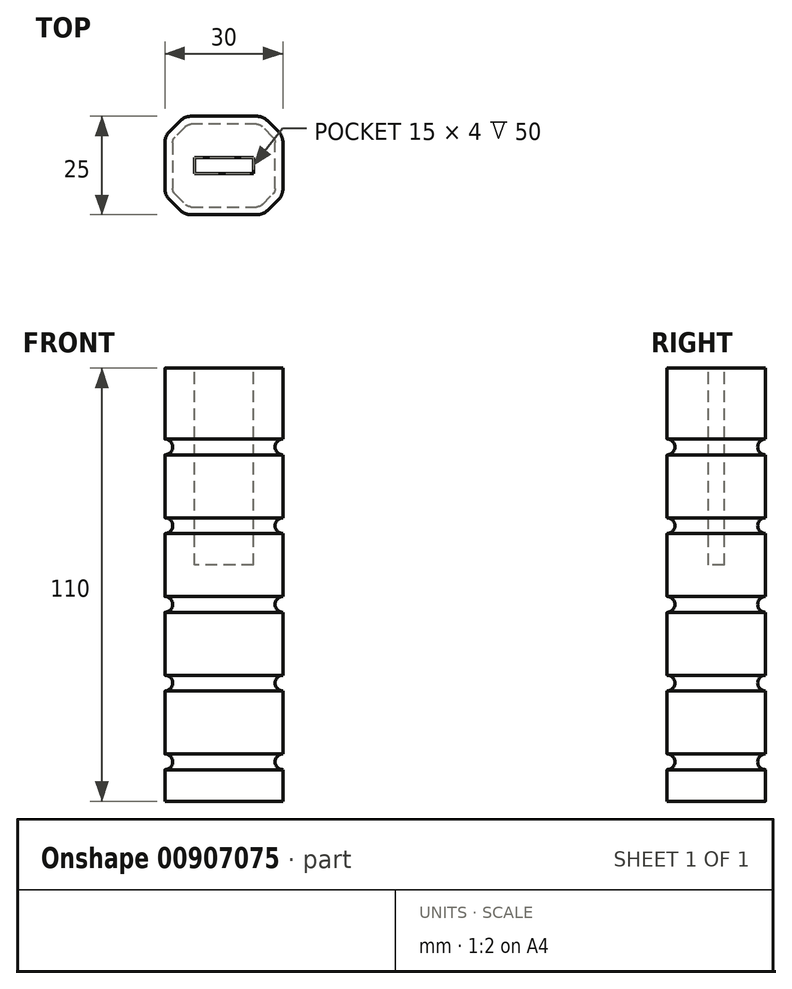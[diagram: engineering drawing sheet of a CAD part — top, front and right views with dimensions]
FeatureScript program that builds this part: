
annotation { "Feature Type Name" : "Feature", "Feature Type Description" : "" }
export const myFeature = defineFeature(function(context is Context, id is Id, definition is map)
    precondition{}
    {
        {
            var Q0;
            Q0=qCreatedBy(makeId("Top.planeOp"),FACE);
            var sketch = newSketch(context, id + "F0", { "sketchPlane" : qUnion([Q0])});
            skLineSegment(sketch, "E0.bottom", {"start": v(15, 12.5) * mm, "end": v(-15, 12.5) * mm});
            skLineSegment(sketch, "E0.top", {"start": v(15, -12.5) * mm, "end": v(-15, -12.5) * mm});
            skLineSegment(sketch, "E0.left", {"start": v(15, 12.5) * mm, "end": v(15, -12.5) * mm});
            skLineSegment(sketch, "E0.right", {"start": v(-15, 12.5) * mm, "end": v(-15, -12.5) * mm});
            skPoint(sketch, "E0.middle", {"position": v(0, 0) * mm});
            skSolve(sketch);
        }
        {
            var Q0;
            Q0 = qSketchRegion(id + "F0", true);
            extrude(context, id + "F1", {"entities" : qUnion([Q0]), "depth" : 110 * mm, "offsetDistance" : 25 * mm});
        }
        {
            var Q0;
            Q0=makeQuery(id+"F1.opExtrude","SWEPT_EDGE",EDGE,{"disambiguationData":[OSD([sQuery(id+"F0.wireOp",EDGE,"E0.top"),sQuery(id+"F0.wireOp",EDGE,"E0.right")])]});
            var Q1;
            Q1=makeQuery(id+"F1.opExtrude","SWEPT_EDGE",EDGE,{"disambiguationData":[OSD([sQuery(id+"F0.wireOp",EDGE,"E0.bottom"),sQuery(id+"F0.wireOp",EDGE,"E0.right")])]});
            var Q2;
            Q2=makeQuery(id+"F1.opExtrude","SWEPT_EDGE",EDGE,{"disambiguationData":[OSD([sQuery(id+"F0.wireOp",EDGE,"E0.top"),sQuery(id+"F0.wireOp",EDGE,"E0.left")])]});
            var Q3;
            Q3=makeQuery(id+"F1.opExtrude","SWEPT_EDGE",EDGE,{"disambiguationData":[OSD([sQuery(id+"F0.wireOp",EDGE,"E0.bottom"),sQuery(id+"F0.wireOp",EDGE,"E0.left")])]});
            chamfer(context, id + "F2", {"entities" : qUnion([Q0, Q1, Q2, Q3]), "width" : 5 * mm, "tangentPropagation" : true});
        }
        {
            var Q0;
            {var subQ0=sQuery(id+"F0.wireOp",EDGE,"E0.top");Q0=makeQuery(id+"F2.opChamfer","BLEND_EDGE",EDGE,{"blendedFrom":[makeQuery(id+"F1.opExtrude","SWEPT_EDGE",EDGE,{"disambiguationData":[OSD([subQ0,sQuery(id+"F0.wireOp",EDGE,"E0.left")])]}),makeQuery(id+"F1.opExtrude","SWEPT_FACE",FACE,{"disambiguationData":[OSD([subQ0])]})],"blendedInto":[makeQuery(id+"F1.opExtrude","SWEPT_FACE",FACE,{"disambiguationData":[OSD([subQ0])]})]});}
            var Q1;
            {var subQ0=sQuery(id+"F0.wireOp",EDGE,"E0.left");Q1=makeQuery(id+"F2.opChamfer","BLEND_EDGE",EDGE,{"blendedFrom":[makeQuery(id+"F1.opExtrude","SWEPT_EDGE",EDGE,{"disambiguationData":[OSD([sQuery(id+"F0.wireOp",EDGE,"E0.top"),subQ0])]}),makeQuery(id+"F1.opExtrude","SWEPT_FACE",FACE,{"disambiguationData":[OSD([subQ0])]})],"blendedInto":[makeQuery(id+"F1.opExtrude","SWEPT_FACE",FACE,{"disambiguationData":[OSD([subQ0])]})]});}
            var Q2;
            {var subQ0=sQuery(id+"F0.wireOp",EDGE,"E0.top");Q2=makeQuery(id+"F2.opChamfer","BLEND_EDGE",EDGE,{"blendedFrom":[makeQuery(id+"F1.opExtrude","SWEPT_EDGE",EDGE,{"disambiguationData":[OSD([subQ0,sQuery(id+"F0.wireOp",EDGE,"E0.right")])]}),makeQuery(id+"F1.opExtrude","SWEPT_FACE",FACE,{"disambiguationData":[OSD([subQ0])]})],"blendedInto":[makeQuery(id+"F1.opExtrude","SWEPT_FACE",FACE,{"disambiguationData":[OSD([subQ0])]})]});}
            var Q3;
            {var subQ0=sQuery(id+"F0.wireOp",EDGE,"E0.right");Q3=makeQuery(id+"F2.opChamfer","BLEND_EDGE",EDGE,{"blendedFrom":[makeQuery(id+"F1.opExtrude","SWEPT_EDGE",EDGE,{"disambiguationData":[OSD([sQuery(id+"F0.wireOp",EDGE,"E0.top"),subQ0])]}),makeQuery(id+"F1.opExtrude","SWEPT_FACE",FACE,{"disambiguationData":[OSD([subQ0])]})],"blendedInto":[makeQuery(id+"F1.opExtrude","SWEPT_FACE",FACE,{"disambiguationData":[OSD([subQ0])]})]});}
            var Q4;
            {var subQ0=sQuery(id+"F0.wireOp",EDGE,"E0.right");Q4=makeQuery(id+"F2.opChamfer","BLEND_EDGE",EDGE,{"blendedFrom":[makeQuery(id+"F1.opExtrude","SWEPT_EDGE",EDGE,{"disambiguationData":[OSD([sQuery(id+"F0.wireOp",EDGE,"E0.bottom"),subQ0])]}),makeQuery(id+"F1.opExtrude","SWEPT_FACE",FACE,{"disambiguationData":[OSD([subQ0])]})],"blendedInto":[makeQuery(id+"F1.opExtrude","SWEPT_FACE",FACE,{"disambiguationData":[OSD([subQ0])]})]});}
            var Q5;
            {var subQ0=sQuery(id+"F0.wireOp",EDGE,"E0.bottom");Q5=makeQuery(id+"F2.opChamfer","BLEND_EDGE",EDGE,{"blendedFrom":[makeQuery(id+"F1.opExtrude","SWEPT_EDGE",EDGE,{"disambiguationData":[OSD([subQ0,sQuery(id+"F0.wireOp",EDGE,"E0.right")])]}),makeQuery(id+"F1.opExtrude","SWEPT_FACE",FACE,{"disambiguationData":[OSD([subQ0])]})],"blendedInto":[makeQuery(id+"F1.opExtrude","SWEPT_FACE",FACE,{"disambiguationData":[OSD([subQ0])]})]});}
            var Q6;
            {var subQ0=sQuery(id+"F0.wireOp",EDGE,"E0.bottom");Q6=makeQuery(id+"F2.opChamfer","BLEND_EDGE",EDGE,{"blendedFrom":[makeQuery(id+"F1.opExtrude","SWEPT_EDGE",EDGE,{"disambiguationData":[OSD([subQ0,sQuery(id+"F0.wireOp",EDGE,"E0.left")])]}),makeQuery(id+"F1.opExtrude","SWEPT_FACE",FACE,{"disambiguationData":[OSD([subQ0])]})],"blendedInto":[makeQuery(id+"F1.opExtrude","SWEPT_FACE",FACE,{"disambiguationData":[OSD([subQ0])]})]});}
            var Q7;
            {var subQ0=sQuery(id+"F0.wireOp",EDGE,"E0.left");Q7=makeQuery(id+"F2.opChamfer","BLEND_EDGE",EDGE,{"blendedFrom":[makeQuery(id+"F1.opExtrude","SWEPT_EDGE",EDGE,{"disambiguationData":[OSD([sQuery(id+"F0.wireOp",EDGE,"E0.bottom"),subQ0])]}),makeQuery(id+"F1.opExtrude","SWEPT_FACE",FACE,{"disambiguationData":[OSD([subQ0])]})],"blendedInto":[makeQuery(id+"F1.opExtrude","SWEPT_FACE",FACE,{"disambiguationData":[OSD([subQ0])]})]});}
            fillet(context, id + "F3", {"entities" : qUnion([Q0, Q1, Q2, Q3, Q4, Q5, Q6, Q7]), "radius" : 4 * mm, "tangentPropagation" : true, "allowEdgeOverflow" : false});
        }
        {
            var Q0;
            Q0=makeQuery(id+"F1.opExtrude","CAP_FACE",FACE,{"disambiguationData":[OSD([sQuery(id+"F0.wireOp",EDGE,"E0.bottom"),sQuery(id+"F0.wireOp",EDGE,"E0.top"),sQuery(id+"F0.wireOp",EDGE,"E0.left"),sQuery(id+"F0.wireOp",EDGE,"E0.right")])],"isStart":false});
            var sketch = newSketch(context, id + "F4", { "sketchPlane" : qUnion([Q0])});
            skLineSegment(sketch, "E1.bottom", {"start": v(7.5, 2) * mm, "end": v(-7.5, 2) * mm});
            skLineSegment(sketch, "E1.top", {"start": v(7.5, -2) * mm, "end": v(-7.5, -2) * mm});
            skLineSegment(sketch, "E1.left", {"start": v(7.5, 2) * mm, "end": v(7.5, -2) * mm});
            skLineSegment(sketch, "E1.right", {"start": v(-7.5, 2) * mm, "end": v(-7.5, -2) * mm});
            skPoint(sketch, "E1.middle", {"position": v(0, 0) * mm});
            skSolve(sketch);
        }
        {
            var Q0;
            Q0 = qSketchRegion(id + "F4", true);
            extrude(context, id + "F5", {"entities" : qUnion([Q0]), "operationType" : NewBodyOperationType.REMOVE, "oppositeDirection" : true, "depth" : 50 * mm, "offsetDistance" : 25 * mm});
        }
        {
            var Q0;
            Q0=makeQuery(id+"F1.opExtrude","CAP_FACE",FACE,{"disambiguationData":[OSD([sQuery(id+"F0.wireOp",EDGE,"E0.bottom"),sQuery(id+"F0.wireOp",EDGE,"E0.top"),sQuery(id+"F0.wireOp",EDGE,"E0.left"),sQuery(id+"F0.wireOp",EDGE,"E0.right")])],"isStart":false});
            cPlane(context, id + "F6", {"entities" : qUnion([Q0]), "cplaneType" : CPlaneType.OFFSET, "offset" : 20 * mm, "oppositeDirection" : true, "width" : 150 * mm, "height" : 150 * mm});
        }
        {
            var Q0;
            Q0=qCreatedBy(id+"F6.planeOp",FACE);
            cPlane(context, id + "F7", {"entities" : qUnion([Q0]), "cplaneType" : CPlaneType.OFFSET, "offset" : 20 * mm, "oppositeDirection" : true, "width" : 150 * mm, "height" : 150 * mm});
        }
        {
            var Q0;
            Q0=qCreatedBy(id+"F7.planeOp",FACE);
            cPlane(context, id + "F8", {"entities" : qUnion([Q0]), "cplaneType" : CPlaneType.OFFSET, "offset" : 20 * mm, "oppositeDirection" : true, "width" : 150 * mm, "height" : 150 * mm});
        }
        {
            var Q0;
            Q0=qCreatedBy(id+"F8.planeOp",FACE);
            cPlane(context, id + "F9", {"entities" : qUnion([Q0]), "cplaneType" : CPlaneType.OFFSET, "offset" : 20 * mm, "oppositeDirection" : true, "width" : 150 * mm, "height" : 150 * mm});
        }
        {
            var Q0;
            Q0=qCreatedBy(id+"F9.planeOp",FACE);
            cPlane(context, id + "F10", {"entities" : qUnion([Q0]), "cplaneType" : CPlaneType.OFFSET, "offset" : 20 * mm, "oppositeDirection" : true, "width" : 150 * mm, "height" : 150 * mm});
        }
        {
            var Q0;
            Q0=qCreatedBy(id+"F6.planeOp",FACE);
            var sketch = newSketch(context, id + "F11", { "sketchPlane" : qUnion([Q0])});
            skLineSegment(sketch, "E2.0.0", {"start": v(-11.17, 11.33) * mm, "end": v(-13.83, 8.67) * mm});
            skArc(sketch, "E2.0.1", {"start": v(-13.83, 8.67) * mm, "mid": v(-14.7, 7.37) * mm, "end": v(-15, 5.84) * mm});
            skLineSegment(sketch, "E2.0.2", {"start": v(-15, 5.84) * mm, "end": v(-15, -5.84) * mm});
            skArc(sketch, "E2.0.3", {"start": v(-15, -5.84) * mm, "mid": v(-14.7, -7.37) * mm, "end": v(-13.83, -8.67) * mm});
            skLineSegment(sketch, "E2.0.4", {"start": v(-13.83, -8.67) * mm, "end": v(-11.17, -11.33) * mm});
            skArc(sketch, "E2.0.5", {"start": v(-11.17, -11.33) * mm, "mid": v(-9.87, -12.2) * mm, "end": v(-8.34, -12.5) * mm});
            skLineSegment(sketch, "E2.0.6", {"start": v(-8.34, -12.5) * mm, "end": v(8.34, -12.5) * mm});
            skArc(sketch, "E2.0.7", {"start": v(8.34, -12.5) * mm, "mid": v(9.87, -12.2) * mm, "end": v(11.17, -11.33) * mm});
            skLineSegment(sketch, "E2.0.8", {"start": v(11.17, -11.33) * mm, "end": v(13.83, -8.67) * mm});
            skArc(sketch, "E2.0.9", {"start": v(13.83, -8.67) * mm, "mid": v(14.7, -7.37) * mm, "end": v(15, -5.84) * mm});
            skLineSegment(sketch, "E2.0.10", {"start": v(15, -5.84) * mm, "end": v(15, 5.84) * mm});
            skArc(sketch, "E2.0.11", {"start": v(15, 5.84) * mm, "mid": v(14.7, 7.37) * mm, "end": v(13.83, 8.67) * mm});
            skLineSegment(sketch, "E2.0.12", {"start": v(13.83, 8.67) * mm, "end": v(11.17, 11.33) * mm});
            skArc(sketch, "E2.0.13", {"start": v(11.17, 11.33) * mm, "mid": v(9.87, 12.2) * mm, "end": v(8.34, 12.5) * mm});
            skLineSegment(sketch, "E2.0.14", {"start": v(8.34, 12.5) * mm, "end": v(-8.34, 12.5) * mm});
            skArc(sketch, "E2.0.15", {"start": v(-8.34, 12.5) * mm, "mid": v(-9.87, 12.2) * mm, "end": v(-11.17, 11.33) * mm});
            skSolve(sketch);
        }
        {
            var Q0;
            Q0=qCreatedBy(id+"F7.planeOp",FACE);
            var sketch = newSketch(context, id + "F12", { "sketchPlane" : qUnion([Q0])});
            skLineSegment(sketch, "E3.0.0", {"start": v(-11.17, 11.33) * mm, "end": v(-13.83, 8.67) * mm});
            skArc(sketch, "E3.0.1", {"start": v(-13.83, 8.67) * mm, "mid": v(-14.7, 7.37) * mm, "end": v(-15, 5.84) * mm});
            skLineSegment(sketch, "E3.0.2", {"start": v(-15, 5.84) * mm, "end": v(-15, -5.84) * mm});
            skArc(sketch, "E3.0.3", {"start": v(-15, -5.84) * mm, "mid": v(-14.7, -7.37) * mm, "end": v(-13.83, -8.67) * mm});
            skLineSegment(sketch, "E3.0.4", {"start": v(-13.83, -8.67) * mm, "end": v(-11.17, -11.33) * mm});
            skArc(sketch, "E3.0.5", {"start": v(-11.17, -11.33) * mm, "mid": v(-9.87, -12.2) * mm, "end": v(-8.34, -12.5) * mm});
            skLineSegment(sketch, "E3.0.6", {"start": v(-8.34, -12.5) * mm, "end": v(8.34, -12.5) * mm});
            skArc(sketch, "E3.0.7", {"start": v(8.34, -12.5) * mm, "mid": v(9.87, -12.2) * mm, "end": v(11.17, -11.33) * mm});
            skLineSegment(sketch, "E3.0.8", {"start": v(11.17, -11.33) * mm, "end": v(13.83, -8.67) * mm});
            skArc(sketch, "E3.0.9", {"start": v(13.83, -8.67) * mm, "mid": v(14.7, -7.37) * mm, "end": v(15, -5.84) * mm});
            skLineSegment(sketch, "E3.0.10", {"start": v(15, -5.84) * mm, "end": v(15, 5.84) * mm});
            skArc(sketch, "E3.0.11", {"start": v(15, 5.84) * mm, "mid": v(14.7, 7.37) * mm, "end": v(13.83, 8.67) * mm});
            skLineSegment(sketch, "E3.0.12", {"start": v(13.83, 8.67) * mm, "end": v(11.17, 11.33) * mm});
            skArc(sketch, "E3.0.13", {"start": v(11.17, 11.33) * mm, "mid": v(9.87, 12.2) * mm, "end": v(8.34, 12.5) * mm});
            skLineSegment(sketch, "E3.0.14", {"start": v(8.34, 12.5) * mm, "end": v(-8.34, 12.5) * mm});
            skArc(sketch, "E3.0.15", {"start": v(-8.34, 12.5) * mm, "mid": v(-9.87, 12.2) * mm, "end": v(-11.17, 11.33) * mm});
            skSolve(sketch);
        }
        {
            var Q0;
            Q0=qCreatedBy(id+"F8.planeOp",FACE);
            var sketch = newSketch(context, id + "F13", { "sketchPlane" : qUnion([Q0])});
            skLineSegment(sketch, "E4.0.0", {"start": v(-11.17, 11.33) * mm, "end": v(-13.83, 8.67) * mm});
            skArc(sketch, "E4.0.1", {"start": v(-13.83, 8.67) * mm, "mid": v(-14.7, 7.37) * mm, "end": v(-15, 5.84) * mm});
            skLineSegment(sketch, "E4.0.2", {"start": v(-15, 5.84) * mm, "end": v(-15, -5.84) * mm});
            skArc(sketch, "E4.0.3", {"start": v(-15, -5.84) * mm, "mid": v(-14.7, -7.37) * mm, "end": v(-13.83, -8.67) * mm});
            skLineSegment(sketch, "E4.0.4", {"start": v(-13.83, -8.67) * mm, "end": v(-11.17, -11.33) * mm});
            skArc(sketch, "E4.0.5", {"start": v(-11.17, -11.33) * mm, "mid": v(-9.87, -12.2) * mm, "end": v(-8.34, -12.5) * mm});
            skLineSegment(sketch, "E4.0.6", {"start": v(-8.34, -12.5) * mm, "end": v(8.34, -12.5) * mm});
            skArc(sketch, "E4.0.7", {"start": v(8.34, -12.5) * mm, "mid": v(9.87, -12.2) * mm, "end": v(11.17, -11.33) * mm});
            skLineSegment(sketch, "E4.0.8", {"start": v(11.17, -11.33) * mm, "end": v(13.83, -8.67) * mm});
            skArc(sketch, "E4.0.9", {"start": v(13.83, -8.67) * mm, "mid": v(14.7, -7.37) * mm, "end": v(15, -5.84) * mm});
            skLineSegment(sketch, "E4.0.10", {"start": v(15, -5.84) * mm, "end": v(15, 5.84) * mm});
            skArc(sketch, "E4.0.11", {"start": v(15, 5.84) * mm, "mid": v(14.7, 7.37) * mm, "end": v(13.83, 8.67) * mm});
            skLineSegment(sketch, "E4.0.12", {"start": v(13.83, 8.67) * mm, "end": v(11.17, 11.33) * mm});
            skArc(sketch, "E4.0.13", {"start": v(11.17, 11.33) * mm, "mid": v(9.87, 12.2) * mm, "end": v(8.34, 12.5) * mm});
            skLineSegment(sketch, "E4.0.14", {"start": v(8.34, 12.5) * mm, "end": v(-8.34, 12.5) * mm});
            skArc(sketch, "E4.0.15", {"start": v(-8.34, 12.5) * mm, "mid": v(-9.87, 12.2) * mm, "end": v(-11.17, 11.33) * mm});
            skSolve(sketch);
        }
        {
            var Q0;
            Q0=qCreatedBy(id+"F9.planeOp",FACE);
            var sketch = newSketch(context, id + "F14", { "sketchPlane" : qUnion([Q0])});
            skLineSegment(sketch, "E5.0.0", {"start": v(-11.17, 11.33) * mm, "end": v(-13.83, 8.67) * mm});
            skArc(sketch, "E5.0.1", {"start": v(-13.83, 8.67) * mm, "mid": v(-14.7, 7.37) * mm, "end": v(-15, 5.84) * mm});
            skLineSegment(sketch, "E5.0.2", {"start": v(-15, 5.84) * mm, "end": v(-15, -5.84) * mm});
            skArc(sketch, "E5.0.3", {"start": v(-15, -5.84) * mm, "mid": v(-14.7, -7.37) * mm, "end": v(-13.83, -8.67) * mm});
            skLineSegment(sketch, "E5.0.4", {"start": v(-13.83, -8.67) * mm, "end": v(-11.17, -11.33) * mm});
            skArc(sketch, "E5.0.5", {"start": v(-11.17, -11.33) * mm, "mid": v(-9.87, -12.2) * mm, "end": v(-8.34, -12.5) * mm});
            skLineSegment(sketch, "E5.0.6", {"start": v(-8.34, -12.5) * mm, "end": v(8.34, -12.5) * mm});
            skArc(sketch, "E5.0.7", {"start": v(8.34, -12.5) * mm, "mid": v(9.87, -12.2) * mm, "end": v(11.17, -11.33) * mm});
            skLineSegment(sketch, "E5.0.8", {"start": v(11.17, -11.33) * mm, "end": v(13.83, -8.67) * mm});
            skArc(sketch, "E5.0.9", {"start": v(13.83, -8.67) * mm, "mid": v(14.7, -7.37) * mm, "end": v(15, -5.84) * mm});
            skLineSegment(sketch, "E5.0.10", {"start": v(15, -5.84) * mm, "end": v(15, 5.84) * mm});
            skArc(sketch, "E5.0.11", {"start": v(15, 5.84) * mm, "mid": v(14.7, 7.37) * mm, "end": v(13.83, 8.67) * mm});
            skLineSegment(sketch, "E5.0.12", {"start": v(13.83, 8.67) * mm, "end": v(11.17, 11.33) * mm});
            skArc(sketch, "E5.0.13", {"start": v(11.17, 11.33) * mm, "mid": v(9.87, 12.2) * mm, "end": v(8.34, 12.5) * mm});
            skLineSegment(sketch, "E5.0.14", {"start": v(8.34, 12.5) * mm, "end": v(-8.34, 12.5) * mm});
            skArc(sketch, "E5.0.15", {"start": v(-8.34, 12.5) * mm, "mid": v(-9.87, 12.2) * mm, "end": v(-11.17, 11.33) * mm});
            skSolve(sketch);
        }
        {
            var Q0;
            Q0=qCreatedBy(id+"F10.planeOp",FACE);
            var sketch = newSketch(context, id + "F15", { "sketchPlane" : qUnion([Q0])});
            skLineSegment(sketch, "E6.0.0", {"start": v(-11.17, 11.33) * mm, "end": v(-13.83, 8.67) * mm});
            skArc(sketch, "E6.0.1", {"start": v(-13.83, 8.67) * mm, "mid": v(-14.7, 7.37) * mm, "end": v(-15, 5.84) * mm});
            skLineSegment(sketch, "E6.0.2", {"start": v(-15, 5.84) * mm, "end": v(-15, -5.84) * mm});
            skArc(sketch, "E6.0.3", {"start": v(-15, -5.84) * mm, "mid": v(-14.7, -7.37) * mm, "end": v(-13.83, -8.67) * mm});
            skLineSegment(sketch, "E6.0.4", {"start": v(-13.83, -8.67) * mm, "end": v(-11.17, -11.33) * mm});
            skArc(sketch, "E6.0.5", {"start": v(-11.17, -11.33) * mm, "mid": v(-9.87, -12.2) * mm, "end": v(-8.34, -12.5) * mm});
            skLineSegment(sketch, "E6.0.6", {"start": v(-8.34, -12.5) * mm, "end": v(8.34, -12.5) * mm});
            skArc(sketch, "E6.0.7", {"start": v(8.34, -12.5) * mm, "mid": v(9.87, -12.2) * mm, "end": v(11.17, -11.33) * mm});
            skLineSegment(sketch, "E6.0.8", {"start": v(11.17, -11.33) * mm, "end": v(13.83, -8.67) * mm});
            skArc(sketch, "E6.0.9", {"start": v(13.83, -8.67) * mm, "mid": v(14.7, -7.37) * mm, "end": v(15, -5.84) * mm});
            skLineSegment(sketch, "E6.0.10", {"start": v(15, -5.84) * mm, "end": v(15, 5.84) * mm});
            skArc(sketch, "E6.0.11", {"start": v(15, 5.84) * mm, "mid": v(14.7, 7.37) * mm, "end": v(13.83, 8.67) * mm});
            skLineSegment(sketch, "E6.0.12", {"start": v(13.83, 8.67) * mm, "end": v(11.17, 11.33) * mm});
            skArc(sketch, "E6.0.13", {"start": v(11.17, 11.33) * mm, "mid": v(9.87, 12.2) * mm, "end": v(8.34, 12.5) * mm});
            skLineSegment(sketch, "E6.0.14", {"start": v(8.34, 12.5) * mm, "end": v(-8.34, 12.5) * mm});
            skArc(sketch, "E6.0.15", {"start": v(-8.34, 12.5) * mm, "mid": v(-9.87, 12.2) * mm, "end": v(-11.17, 11.33) * mm});
            skSolve(sketch);
        }
        {
            var Q0;
            Q0=qCreatedBy(makeId("Front.planeOp"),FACE);
            var sketch = newSketch(context, id + "F16", { "sketchPlane" : qUnion([Q0])});
            skCircle(sketch, "E7", {"center": v(-15, 90) * mm, "radius": 2 * mm});
            skCircle(sketch, "E8", {"center": v(-15, 70) * mm, "radius": 2 * mm});
            skCircle(sketch, "E9", {"center": v(-15, 50) * mm, "radius": 2 * mm});
            skCircle(sketch, "E10", {"center": v(-15, 30) * mm, "radius": 2 * mm});
            skCircle(sketch, "E11", {"center": v(-15, 10) * mm, "radius": 2 * mm});
            skSolve(sketch);
        }
        {
            var Q0;
            Q0 = qSketchRegion(id + "F16", true);
            var Q1;
            Q1 = qConstructionFilter(qBodyType(qCreatedBy(id + "F11" ,EDGE), BodyType.WIRE), ConstructionObject.NO);
            sweep(context, id + "F17", {"operationType" : NewBodyOperationType.REMOVE, "profiles" : qUnion([Q0]), "path" : qUnion([Q1])});
        }
    });
